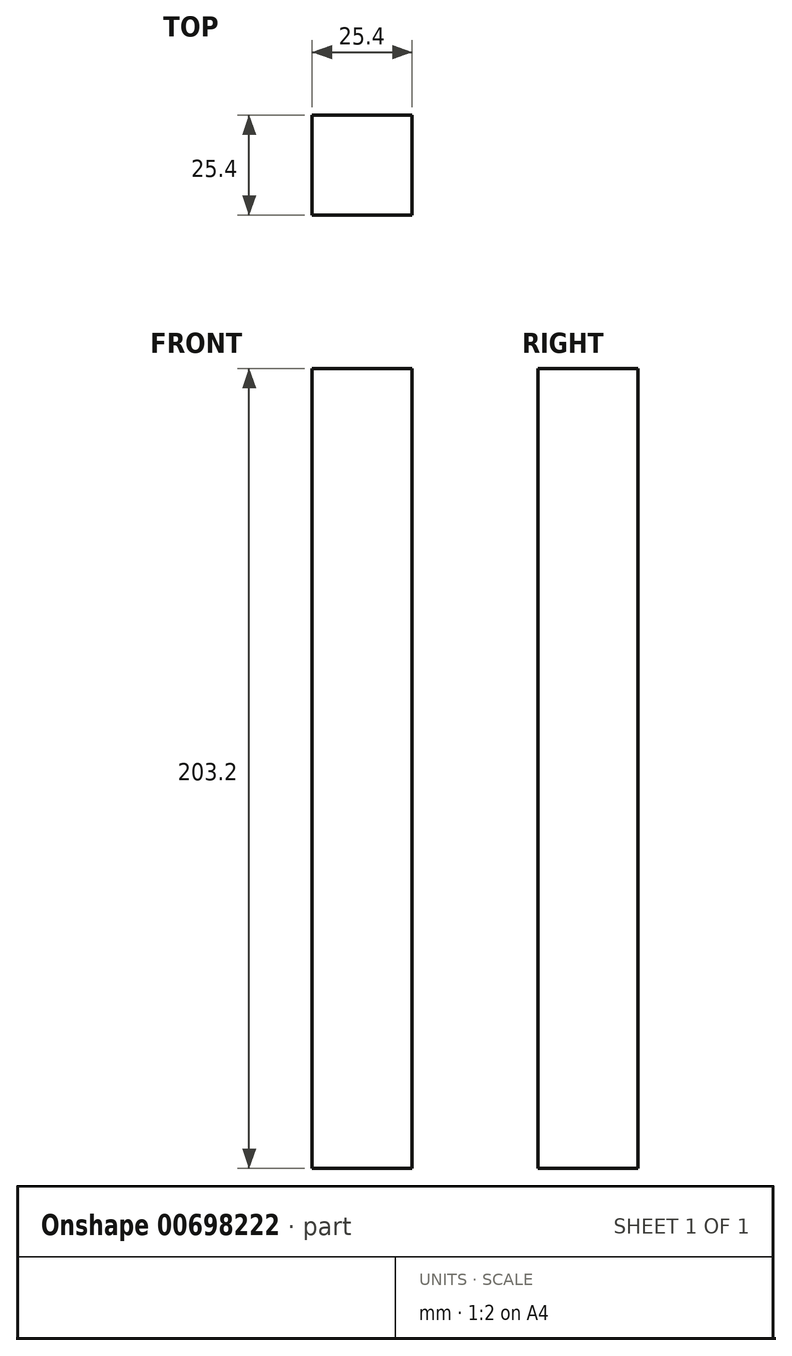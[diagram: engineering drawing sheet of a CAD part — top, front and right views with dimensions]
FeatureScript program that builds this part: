
annotation { "Feature Type Name" : "Feature", "Feature Type Description" : "" }
export const myFeature = defineFeature(function(context is Context, id is Id, definition is map)
    precondition{}
    {
        {
            var Q0;
            Q0=qCreatedBy(makeId("Right.planeOp"),FACE);
            var sketch = newSketch(context, id + "F0", { "sketchPlane" : qUnion([Q0])});
            skLineSegment(sketch, "E0.bottom", {"start": v(-58.92, 86.8) * mm, "end": v(93.48, 86.8) * mm});
            skLineSegment(sketch, "E0.top", {"start": v(-58.92, -65.6) * mm, "end": v(93.48, -65.6) * mm});
            skLineSegment(sketch, "E0.left", {"start": v(-58.92, 86.8) * mm, "end": v(-58.92, -65.6) * mm});
            skLineSegment(sketch, "E0.right", {"start": v(93.48, 86.8) * mm, "end": v(93.48, -65.6) * mm});
            skLineSegment(sketch, "E1.bottom", {"start": v(93.48, -65.6) * mm, "end": v(93.48, -65.6) * mm});
            skLineSegment(sketch, "E1.top", {"start": v(93.48, 22.38) * mm, "end": v(93.48, 22.38) * mm});
            skLineSegment(sketch, "E1.left", {"start": v(93.48, -65.6) * mm, "end": v(93.48, 22.38) * mm});
            skLineSegment(sketch, "E1.right", {"start": v(93.48, -65.6) * mm, "end": v(93.48, 22.38) * mm});
            skSolve(sketch);
        }
        {
            var Q0;
            Q0=makeQuery(id+"F0.imprint","IMPRINT",FACE,{"disambiguationData":[TD([[makeQuery(id+"F0.imprint","IMPRINT",EDGE,{"derivedFrom":sQuery(id+"F0.wireOp",EDGE,"E0.bottom")}),-1.0]])]});
            extrude(context, id + "F1", {"entities" : qUnion([Q0]), "depth" : 25.4 * mm, "offsetDistance" : 25.4 * mm});
        }
        {
            var Q0;
            Q0=makeQuery(id+"F1.opExtrude","SWEPT_BODY",BODY,{"disambiguationData":[OSD([sQuery(id+"F0.wireOp",EDGE,"E0.bottom"),sQuery(id+"F0.wireOp",EDGE,"E0.top"),sQuery(id+"F0.wireOp",EDGE,"E0.left"),sQuery(id+"F0.wireOp",EDGE,"E0.right"),sQuery(id+"F0.wireOp",EDGE,"E1.right")])]});
            deleteBodies(context, id + "F2", {"entities" : qUnion([Q0])});
        }
        {
            var Q0;
            Q0=qCreatedBy(makeId("Front.planeOp"),FACE);
            var sketch = newSketch(context, id + "F3", { "sketchPlane" : qUnion([Q0])});
            skLineSegment(sketch, "E2.bottom", {"start": v(-98.45, 110.86) * mm, "end": v(-73.05, 110.86) * mm});
            skLineSegment(sketch, "E2.top", {"start": v(-98.45, -92.34) * mm, "end": v(-73.05, -92.34) * mm});
            skLineSegment(sketch, "E2.left", {"start": v(-98.45, 110.86) * mm, "end": v(-98.45, -92.34) * mm});
            skLineSegment(sketch, "E2.right", {"start": v(-73.05, 110.86) * mm, "end": v(-73.05, -92.34) * mm});
            skSolve(sketch);
        }
        {
            var Q0;
            Q0=makeQuery(id+"F3.imprint","IMPRINT",FACE,{"disambiguationData":[TD([[makeQuery(id+"F3.imprint","IMPRINT",EDGE,{"derivedFrom":sQuery(id+"F3.wireOp",EDGE,"E2.bottom")}),-1.0]])]});
            extrude(context, id + "F4", {"entities" : qUnion([Q0]), "depth" : 25.4 * mm, "offsetDistance" : 25.4 * mm});
        }
    });
